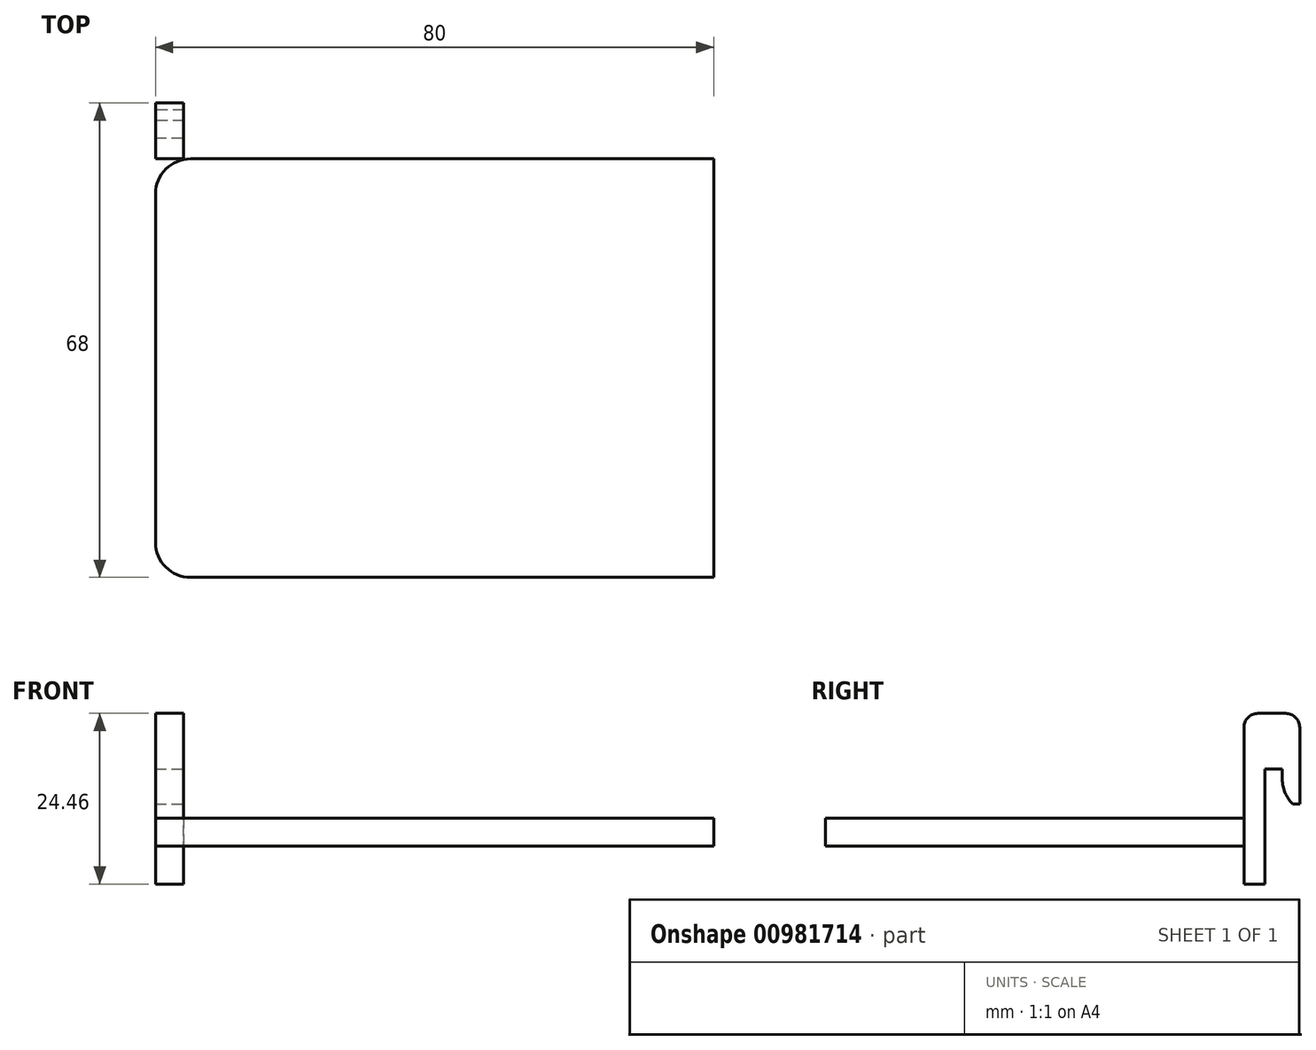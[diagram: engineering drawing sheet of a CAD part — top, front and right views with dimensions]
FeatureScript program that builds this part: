
annotation { "Feature Type Name" : "Feature", "Feature Type Description" : "" }
export const myFeature = defineFeature(function(context is Context, id is Id, definition is map)
    precondition{}
    {
        {
            var Q0;
            Q0=qCreatedBy(makeId("Front.planeOp"),FACE);
            var sketch = newSketch(context, id + "F0", { "sketchPlane" : qUnion([Q0])});
            skLineSegment(sketch, "E0", {"start": v(-25.52, 25.62) * mm, "end": v(74.48, 25.62) * mm, "construction": true});
            skLineSegment(sketch, "E1", {"start": v(-25.52, 13.62) * mm, "end": v(74.48, 13.62) * mm, "construction": true});
            skLineSegment(sketch, "E2", {"start": v(-25.8, 6.62) * mm, "end": v(74.2, 6.62) * mm, "construction": true});
            skLineSegment(sketch, "E3", {"start": v(-25.8, -10.38) * mm, "end": v(74.2, -10.38) * mm, "construction": true});
            skLineSegment(sketch, "E4", {"start": v(-25.5, 25.12) * mm, "end": v(74.5, 25.12) * mm, "construction": true});
            skLineSegment(sketch, "E5", {"start": v(-25.52, 14.12) * mm, "end": v(74.48, 14.12) * mm, "construction": true});
            skSolve(sketch);
        }
        {
            var Q0;
            Q0=qCreatedBy(makeId("Front.planeOp"),FACE);
            var sketch = newSketch(context, id + "F1", { "sketchPlane" : qUnion([Q0])});
            skLineSegment(sketch, "E6.0", {"start": v(-25.52, 25.62) * mm, "end": v(74.48, 25.62) * mm, "construction": true});
            skLineSegment(sketch, "E7.0", {"start": v(-25.5, 25.12) * mm, "end": v(74.5, 25.12) * mm, "construction": true});
            skLineSegment(sketch, "E8.0", {"start": v(-25.52, 14.12) * mm, "end": v(74.48, 14.12) * mm, "construction": true});
            skLineSegment(sketch, "E9.0", {"start": v(-25.52, 13.62) * mm, "end": v(74.48, 13.62) * mm, "construction": true});
            skLineSegment(sketch, "E10.0", {"start": v(-25.8, 6.62) * mm, "end": v(74.2, 6.62) * mm, "construction": true});
            skLineSegment(sketch, "E11.0", {"start": v(-25.8, -10.38) * mm, "end": v(74.2, -10.38) * mm, "construction": true});
            skLineSegment(sketch, "E12", {"start": v(-25.52, 25.62) * mm, "end": v(-25.8, -10.38) * mm, "construction": true});
            skLineSegment(sketch, "E13", {"start": v(74.48, 25.62) * mm, "end": v(74.2, -10.38) * mm, "construction": true});
            skSolve(sketch);
        }
        {
            var Q0;
            Q0=qCreatedBy(makeId("Front.planeOp"),FACE);
            var sketch = newSketch(context, id + "F2", { "sketchPlane" : qUnion([Q0])});
            skLineSegment(sketch, "E14.0", {"start": v(-25.5, 25.12) * mm, "end": v(74.5, 25.12) * mm, "construction": true});
            skLineSegment(sketch, "E15.0", {"start": v(-25.52, 14.12) * mm, "end": v(74.48, 14.12) * mm, "construction": true});
            skLineSegment(sketch, "E16.0", {"start": v(-25.8, 6.62) * mm, "end": v(74.2, 6.62) * mm, "construction": true});
            skLineSegment(sketch, "E17.bottom", {"start": v(-18.06, 25.12) * mm, "end": v(-14.06, 25.12) * mm});
            skLineSegment(sketch, "E17.top", {"start": v(-18.06, 14.12) * mm, "end": v(-14.06, 14.12) * mm});
            skLineSegment(sketch, "E17.left", {"start": v(-18.06, 25.12) * mm, "end": v(-18.06, 14.12) * mm});
            skLineSegment(sketch, "E17.right", {"start": v(-14.06, 25.12) * mm, "end": v(-14.06, 14.12) * mm});
            skSolve(sketch);
        }
        {
            var Q0;
            Q0=makeQuery(id+"F2.imprint","IMPRINT",FACE,{"disambiguationData":[TD([[makeQuery(id+"F2.imprint","IMPRINT",EDGE,{"derivedFrom":sQuery(id+"F2.wireOp",EDGE,"E17.bottom")}),-1.0]])]});
            extrude(context, id + "F3", {"entities" : qUnion([Q0]), "endBound" : BoundingType.SYMMETRIC, "depth" : 8 * mm, "offsetDistance" : 25 * mm});
        }
        {
            var Q0;
            Q0=makeQuery(id+"F3.opExtrude","SWEPT_FACE",FACE,{"disambiguationData":[OSD([sQuery(id+"F2.wireOp",EDGE,"E17.top")])]});
            var sketch = newSketch(context, id + "F4", { "sketchPlane" : qUnion([Q0])});
            skLineSegment(sketch, "E18.0", {"start": v(-18.06, 4) * mm, "end": v(-18.06, 1) * mm});
            skLineSegment(sketch, "E19.0", {"start": v(-18.06, 4) * mm, "end": v(-14.06, 4) * mm});
            skLineSegment(sketch, "E20.0", {"start": v(-14.06, 4) * mm, "end": v(-14.06, 1) * mm});
            skLineSegment(sketch, "E21", {"start": v(-18.06, 1) * mm, "end": v(-14.06, 1) * mm});
            skPoint(sketch, "E22.orphan", {"position": v(-18.06, -4) * mm});
            skPoint(sketch, "E23.orphan", {"position": v(-14.06, -4) * mm});
            skSolve(sketch);
        }
        {
            var Q0;
            Q0=makeQuery(id+"F4.imprint","IMPRINT",FACE,{"disambiguationData":[TD([[makeQuery(id+"F4.imprint","IMPRINT",EDGE,{"derivedFrom":sQuery(id+"F4.wireOp",EDGE,"E18.0")}),1.0]])]});
            extrude(context, id + "F5", {"entities" : qUnion([Q0]), "operationType" : NewBodyOperationType.ADD, "depth" : 25 * mm, "offsetDistance" : 25 * mm});
        }
        {
            var Q0;
            Q0=makeQuery(id+"F3.opExtrude","SWEPT_FACE",FACE,{"disambiguationData":[OSD([sQuery(id+"F2.wireOp",EDGE,"E17.top")])]});
            var sketch = newSketch(context, id + "F6", { "sketchPlane" : qUnion([Q0])});
            skLineSegment(sketch, "E24.0", {"start": v(-14.06, 1) * mm, "end": v(-14.06, -4) * mm});
            skLineSegment(sketch, "E25.0", {"start": v(-18.06, -4) * mm, "end": v(-14.06, -4) * mm});
            skLineSegment(sketch, "E26.0", {"start": v(-18.06, 1) * mm, "end": v(-18.06, -4) * mm});
            skLineSegment(sketch, "E27", {"start": v(-14.06, -1.5) * mm, "end": v(-18.06, -1.5) * mm});
            skSolve(sketch);
        }
        {
            var Q0;
            {var subQ0=sQuery(id+"F6.wireOp",EDGE,"E25.0");Q0=makeQuery(id+"F6.imprint","IMPRINT",FACE,{"disambiguationData":[TD([[makeQuery(id+"F6.imprint","IMPRINT",EDGE,{"derivedFrom":subQ0}),1.0]])]});}
            extrude(context, id + "F7", {"entities" : qUnion([Q0]), "operationType" : NewBodyOperationType.ADD, "depth" : 5 * mm, "offsetDistance" : 25 * mm});
        }
        {
            var Q0;
            Q0=makeQuery(id+"F7.opExtrude","CAP_EDGE",EDGE,{"disambiguationData":[OSD([sQuery(id+"F6.wireOp",EDGE,"E27")])],"isStart":false});
            chamfer(context, id + "F8", {"entities" : qUnion([Q0]), "chamferType" : ChamferType.TWO_OFFSETS, "width1" : 1.5 * mm, "oppositeDirection" : false, "width2" : 1 * mm, "tangentPropagation" : true});
        }
        {
            var Q0;
            {var subQ0=sQuery(id+"F6.wireOp",EDGE,"E27");Q0=makeQuery(id+"F8.opChamfer","BLEND_EDGE",EDGE,{"blendedFrom":[makeQuery(id+"F7.opExtrude","CAP_EDGE",EDGE,{"disambiguationData":[OSD([subQ0])],"isStart":false}),makeQuery(id+"F7.opExtrude","SWEPT_FACE",FACE,{"disambiguationData":[OSD([subQ0])]})],"blendedInto":[makeQuery(id+"F7.opExtrude","SWEPT_FACE",FACE,{"disambiguationData":[OSD([subQ0])]})]});}
            fillet(context, id + "F9", {"entities" : qUnion([Q0]), "radius" : 5 * mm, "tangentPropagation" : true, "allowEdgeOverflow" : false});
        }
        {
            var Q0;
            Q0=makeQuery(id+"F3.opExtrude","CAP_EDGE",EDGE,{"disambiguationData":[OSD([sQuery(id+"F2.wireOp",EDGE,"E17.bottom")])],"isStart":true});
            fillet(context, id + "F10", {"entities" : qUnion([Q0]), "radius" : 5 * mm, "tangentPropagation" : true, "allowEdgeOverflow" : false});
        }
        {
            var Q0;
            Q0=makeQuery(id+"F5.boolean.opBoolean","MERGE",FACE,{"derivedFrom":[makeQuery(id+"F3.opExtrude","CAP_FACE",FACE,{"disambiguationData":[OSD([sQuery(id+"F2.wireOp",EDGE,"E17.bottom"),sQuery(id+"F2.wireOp",EDGE,"E17.top"),sQuery(id+"F2.wireOp",EDGE,"E17.left"),sQuery(id+"F2.wireOp",EDGE,"E17.right")])],"isStart":false}),makeQuery(id+"F5.opExtrude","SWEPT_FACE",FACE,{"disambiguationData":[OSD([sQuery(id+"F4.wireOp",EDGE,"E19.0")])]})]});
            var sketch = newSketch(context, id + "F11", { "sketchPlane" : qUnion([Q0])});
            skLineSegment(sketch, "E28.bottom", {"start": v(-18.06, 7.12) * mm, "end": v(61.94, 7.12) * mm});
            skLineSegment(sketch, "E28.top", {"start": v(-18.06, 3.12) * mm, "end": v(61.94, 3.12) * mm});
            skLineSegment(sketch, "E28.left", {"start": v(-18.06, 7.12) * mm, "end": v(-18.06, 3.12) * mm});
            skLineSegment(sketch, "E28.right", {"start": v(61.94, 7.12) * mm, "end": v(61.94, 3.12) * mm});
            skSolve(sketch);
        }
        {
            var Q0;
            {var subQ0=sQuery(id+"F11.wireOp",EDGE,"E28.left");Q0=makeQuery(id+"F11.imprint","IMPRINT",FACE,{"disambiguationData":[TD([[makeQuery(id+"F11.imprint","IMPRINT",EDGE,{"derivedFrom":subQ0}),1.0]])]});}
            var Q1;
            {var subQ0=sQuery(id+"F11.wireOp",EDGE,"E28.right");Q1=makeQuery(id+"F11.imprint","IMPRINT",FACE,{"disambiguationData":[TD([[makeQuery(id+"F11.imprint","IMPRINT",EDGE,{"derivedFrom":subQ0}),-1.0]])]});}
            extrude(context, id + "F12", {"entities" : qUnion([Q0, Q1]), "depth" : 60 * mm, "offsetDistance" : 25 * mm});
        }
        {
            var Q0;
            Q0=makeQuery(id+"F5.opExtrude","CAP_FACE",FACE,{"disambiguationData":[OSD([sQuery(id+"F4.wireOp",EDGE,"E18.0"),sQuery(id+"F4.wireOp",EDGE,"E19.0"),sQuery(id+"F4.wireOp",EDGE,"E20.0"),sQuery(id+"F4.wireOp",EDGE,"E21")])],"isStart":false});
            cPlane(context, id + "F13", {"entities" : qUnion([Q0]), "cplaneType" : CPlaneType.OFFSET, "offset" : 8.54 * mm, "oppositeDirection" : true, "width" : 150 * mm, "height" : 150 * mm});
        }
        {
            var Q0;
            Q0=qCreatedBy(id+"F13.planeOp",FACE);
            var sketch = newSketch(context, id + "F14", { "sketchPlane" : qUnion([Q0])});
            skLineSegment(sketch, "E29.bottom", {"start": v(-10.8, 6.79) * mm, "end": v(-23.48, 6.79) * mm});
            skLineSegment(sketch, "E29.top", {"start": v(-10.8, -6.97) * mm, "end": v(-23.48, -6.97) * mm});
            skLineSegment(sketch, "E29.left", {"start": v(-10.8, 6.79) * mm, "end": v(-10.8, -6.97) * mm});
            skLineSegment(sketch, "E29.right", {"start": v(-23.48, 6.79) * mm, "end": v(-23.48, -6.97) * mm});
            skSolve(sketch);
        }
        {
            var Q0;
            Q0=makeQuery(id+"F14.imprint","IMPRINT",FACE,{"disambiguationData":[TD([[makeQuery(id+"F14.imprint","IMPRINT",EDGE,{"derivedFrom":sQuery(id+"F14.wireOp",EDGE,"E29.bottom")}),1.0]])]});
            extrude(context, id + "F15", {"entities" : qUnion([Q0]), "operationType" : NewBodyOperationType.REMOVE, "depth" : 25 * mm, "offsetDistance" : 25 * mm});
        }
        {
            var Q0;
            Q0=makeQuery(id+"F3.opExtrude","CAP_EDGE",EDGE,{"disambiguationData":[OSD([sQuery(id+"F2.wireOp",EDGE,"E17.bottom")])],"isStart":false});
            fillet(context, id + "F16", {"entities" : qUnion([Q0]), "radius" : 2 * mm, "tangentPropagation" : true, "allowEdgeOverflow" : false});
        }
        {
            var Q0;
            Q0=makeQuery(id+"F12.opExtrude","CAP_EDGE",EDGE,{"disambiguationData":[OSD([sQuery(id+"F11.wireOp",EDGE,"E28.left")])],"isStart":true});
            var Q1;
            Q1=makeQuery(id+"F12.opExtrude","CAP_EDGE",EDGE,{"disambiguationData":[OSD([sQuery(id+"F11.wireOp",EDGE,"E28.left")])],"isStart":false});
            fillet(context, id + "F17", {"entities" : qUnion([Q0, Q1]), "radius" : 5 * mm, "tangentPropagation" : true, "allowEdgeOverflow" : false});
        }
        {
            var Q0;
            Q0=makeQuery(id+"F3.opExtrude","SWEPT_FACE",FACE,{"disambiguationData":[OSD([sQuery(id+"F2.wireOp",EDGE,"E17.bottom")])]});
            cPlane(context, id + "F18", {"entities" : qUnion([Q0]), "cplaneType" : CPlaneType.OFFSET, "offset" : 3 * mm, "oppositeDirection" : true, "width" : 150 * mm, "height" : 150 * mm});
        }
        {
            var Q0;
            Q0=qCreatedBy(id+"F18.planeOp",FACE);
            var sketch = newSketch(context, id + "F19", { "sketchPlane" : qUnion([Q0])});
            skLineSegment(sketch, "E30.bottom", {"start": v(-2.97, 13.2) * mm, "end": v(-23.43, 13.2) * mm});
            skLineSegment(sketch, "E30.top", {"start": v(-2.97, -10.09) * mm, "end": v(-23.43, -10.09) * mm});
            skLineSegment(sketch, "E30.left", {"start": v(-2.97, 13.2) * mm, "end": v(-2.97, -10.09) * mm});
            skLineSegment(sketch, "E30.right", {"start": v(-23.43, 13.2) * mm, "end": v(-23.43, -10.09) * mm});
            skSolve(sketch);
        }
        {
            var Q0;
            Q0=makeQuery(id+"F19.imprint","IMPRINT",FACE,{"disambiguationData":[TD([[makeQuery(id+"F19.imprint","IMPRINT",EDGE,{"derivedFrom":sQuery(id+"F19.wireOp",EDGE,"E30.bottom")}),1.0]])]});
            extrude(context, id + "F20", {"entities" : qUnion([Q0]), "operationType" : NewBodyOperationType.REMOVE, "depth" : 25 * mm, "offsetDistance" : 25 * mm});
        }
        {
            var Q0;
            Q0=makeQuery(id+"F20.boolean.opBoolean","INTERSECT",EDGE,{"derivedFrom":[makeQuery(id+"F5.boolean.opBoolean","MERGE",FACE,{"derivedFrom":[makeQuery(id+"F3.opExtrude","CAP_FACE",FACE,{"disambiguationData":[OSD([sQuery(id+"F2.wireOp",EDGE,"E17.bottom"),sQuery(id+"F2.wireOp",EDGE,"E17.top"),sQuery(id+"F2.wireOp",EDGE,"E17.left"),sQuery(id+"F2.wireOp",EDGE,"E17.right")])],"isStart":false}),makeQuery(id+"F5.opExtrude","SWEPT_FACE",FACE,{"disambiguationData":[OSD([sQuery(id+"F4.wireOp",EDGE,"E19.0")])]})]}),makeQuery(id+"F20.opExtrude","CAP_FACE",FACE,{"disambiguationData":[OSD([sQuery(id+"F19.wireOp",EDGE,"E30.bottom"),sQuery(id+"F19.wireOp",EDGE,"E30.top"),sQuery(id+"F19.wireOp",EDGE,"E30.left"),sQuery(id+"F19.wireOp",EDGE,"E30.right")])],"isStart":true})]});
            var Q1;
            Q1=makeQuery(id+"F20.boolean.opBoolean","INTERSECT",EDGE,{"derivedFrom":[makeQuery(id+"F10.opFillet","BLEND_FACE",FACE,{"disambiguationData":[OSD([sQuery(id+"F2.wireOp",EDGE,"E17.bottom")])]}),makeQuery(id+"F20.opExtrude","CAP_FACE",FACE,{"disambiguationData":[OSD([sQuery(id+"F19.wireOp",EDGE,"E30.bottom"),sQuery(id+"F19.wireOp",EDGE,"E30.top"),sQuery(id+"F19.wireOp",EDGE,"E30.left"),sQuery(id+"F19.wireOp",EDGE,"E30.right")])],"isStart":true})]});
            fillet(context, id + "F21", {"entities" : qUnion([Q0, Q1]), "radius" : 2 * mm, "tangentPropagation" : true, "allowEdgeOverflow" : false});
        }
    });
